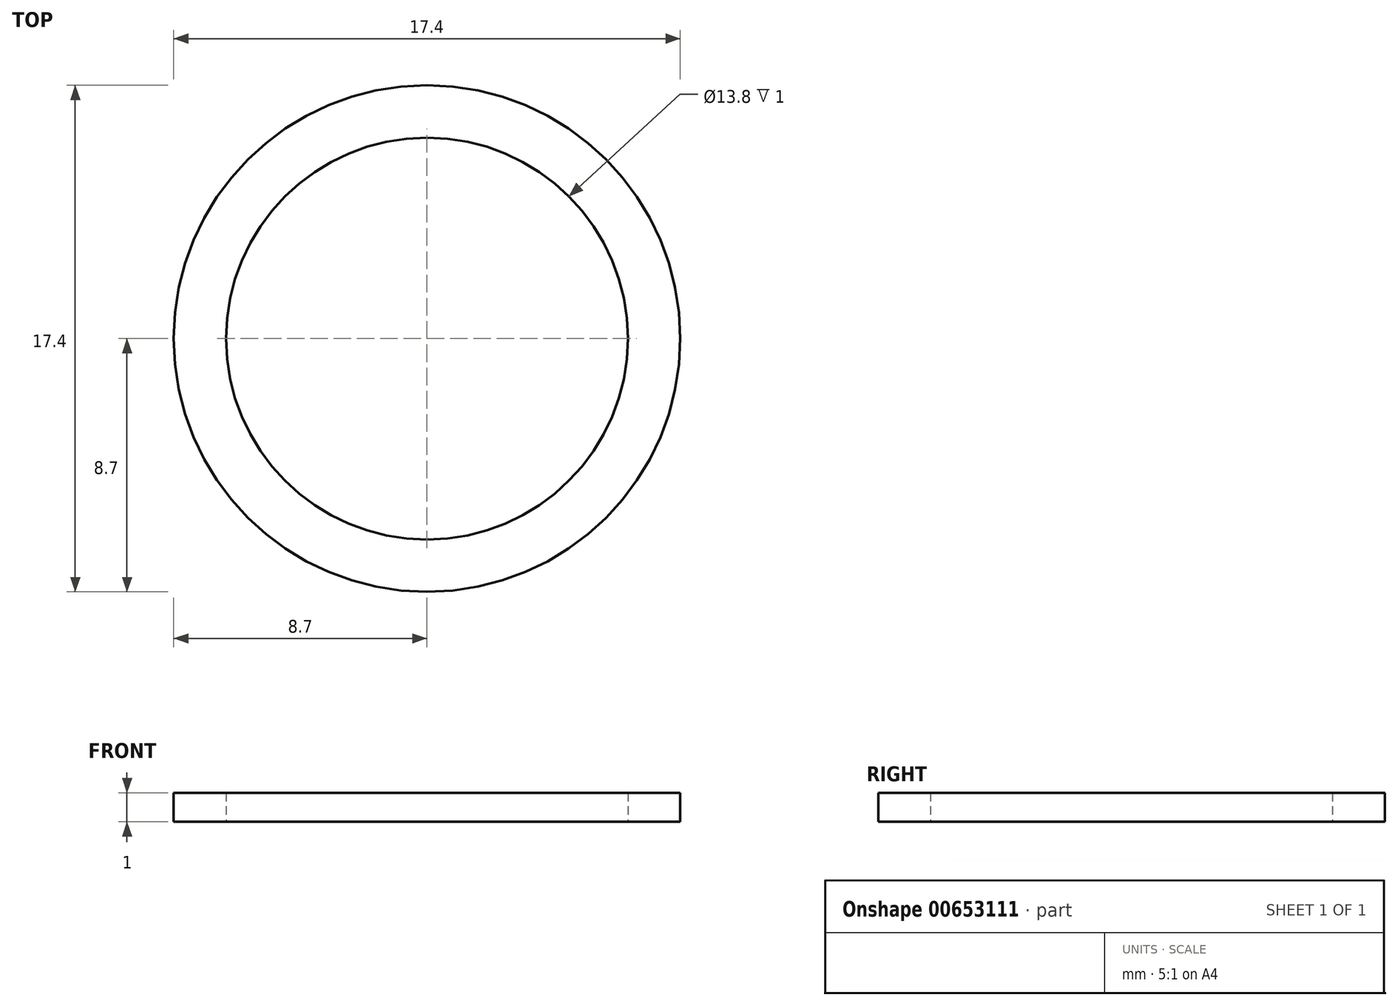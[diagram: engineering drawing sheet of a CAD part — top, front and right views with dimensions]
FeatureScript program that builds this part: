
annotation { "Feature Type Name" : "Feature", "Feature Type Description" : "" }
export const myFeature = defineFeature(function(context is Context, id is Id, definition is map)
    precondition{}
    {
        {
            var Q0;
            Q0=qCreatedBy(makeId("Top.planeOp"),FACE);
            var sketch = newSketch(context, id + "F0", { "sketchPlane" : qUnion([Q0])});
            skCircle(sketch, "E0", {"center": v(0, 0) * mm, "radius": 6.9 * mm});
            skCircle(sketch, "E1", {"center": v(0, 0) * mm, "radius": 8.7 * mm});
            skSolve(sketch);
        }
        {
            var Q0;
            Q0 = qSketchRegion(id + "F0", true);
            extrude(context, id + "F1", {"entities" : qUnion([Q0]), "depth" : 1 * mm, "offsetDistance" : 25 * mm});
        }
    });
